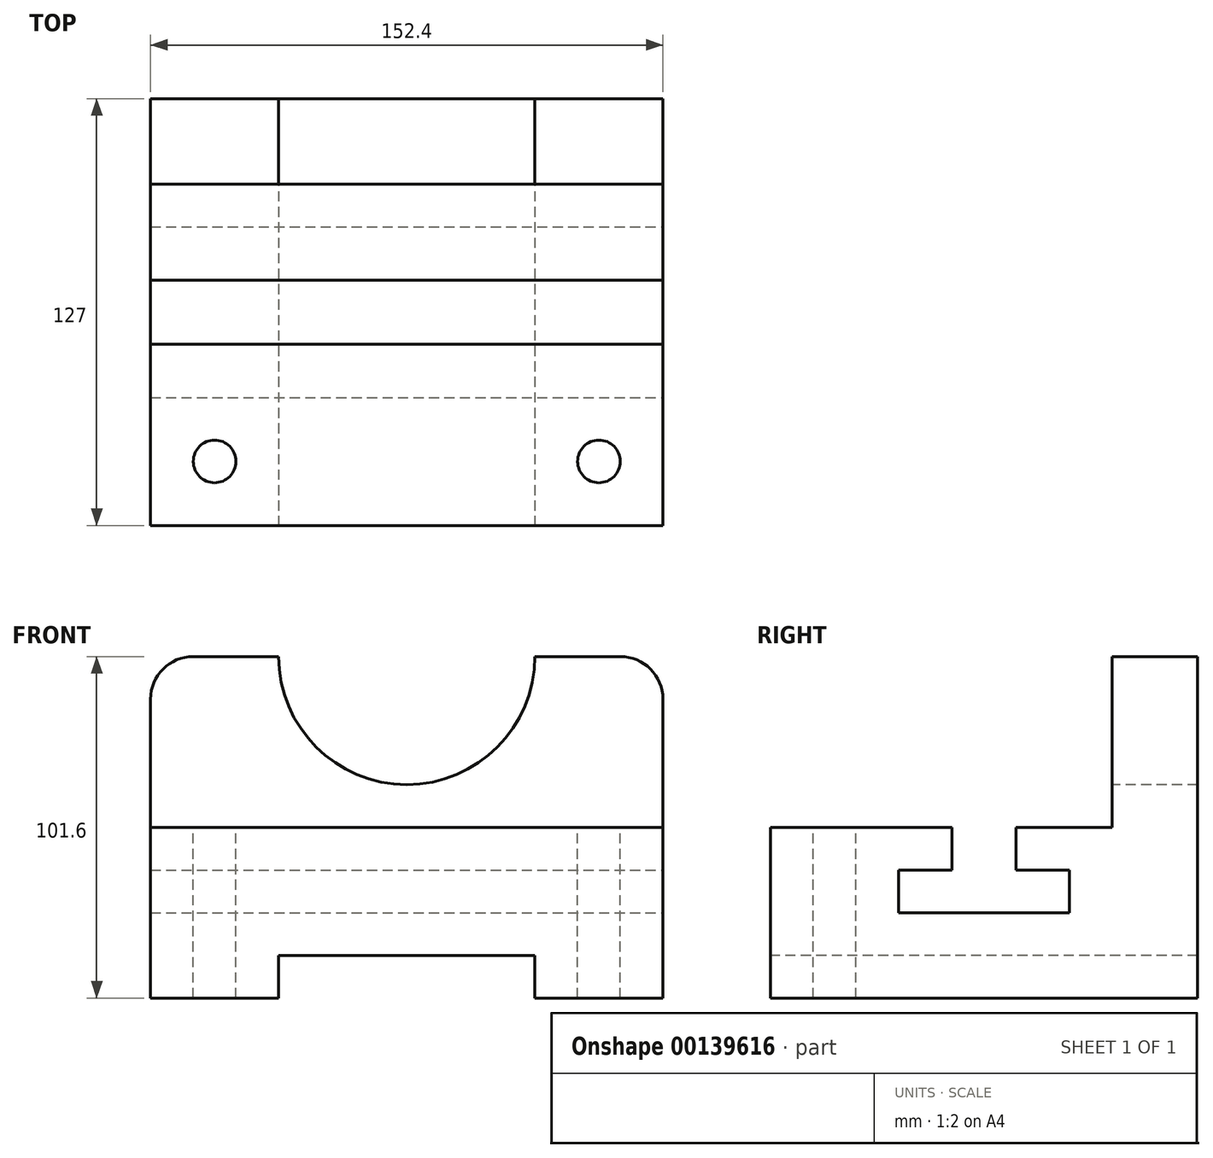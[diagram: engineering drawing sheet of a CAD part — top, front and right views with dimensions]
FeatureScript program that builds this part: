
annotation { "Feature Type Name" : "Feature", "Feature Type Description" : "" }
export const myFeature = defineFeature(function(context is Context, id is Id, definition is map)
    precondition{}
    {
        {
            var Q0;
            Q0=qCreatedBy(makeId("Front.planeOp"),FACE);
            var sketch = newSketch(context, id + "F0", { "sketchPlane" : qUnion([Q0])});
            skLineSegment(sketch, "E0", {"start": v(-76.3, 0) * mm, "end": v(76.1, 0) * mm});
            skLineSegment(sketch, "E1", {"start": v(76.1, 0) * mm, "end": v(76.1, 50.8) * mm});
            skLineSegment(sketch, "E2", {"start": v(76.1, 50.8) * mm, "end": v(-76.3, 50.8) * mm});
            skLineSegment(sketch, "E3", {"start": v(-76.3, 50.8) * mm, "end": v(-76.3, 0) * mm});
            skSolve(sketch);
        }
        {
            var Q0;
            Q0 = qSketchRegion(id + "F0", true);
            extrude(context, id + "F1", {"entities" : qUnion([Q0]), "endBound" : BoundingType.SYMMETRIC, "depth" : 127 * mm});
        }
        {
            var Q0;
            Q0=makeQuery(id+"F1.opExtrude","CAP_FACE",FACE,{"disambiguationData":[OSD([sQuery(id+"F0.wireOp",EDGE,"E0"),sQuery(id+"F0.wireOp",EDGE,"E1"),sQuery(id+"F0.wireOp",EDGE,"E2"),sQuery(id+"F0.wireOp",EDGE,"E3")])],"isStart":false});
            var sketch = newSketch(context, id + "F2", { "sketchPlane" : qUnion([Q0])});
            skLineSegment(sketch, "E4", {"start": v(-76.3, 0) * mm, "end": v(-38.2, 0) * mm});
            skLineSegment(sketch, "E5", {"start": v(76.1, 0) * mm, "end": v(38, 0) * mm});
            skLineSegment(sketch, "E6", {"start": v(38, 0) * mm, "end": v(-38.2, 0) * mm});
            skLineSegment(sketch, "E7", {"start": v(-38.2, 0) * mm, "end": v(-38.2, 12.7) * mm});
            skLineSegment(sketch, "E8", {"start": v(38, 0) * mm, "end": v(38, 12.7) * mm});
            skLineSegment(sketch, "E9", {"start": v(-38.2, 12.7) * mm, "end": v(38, 12.7) * mm});
            skSolve(sketch);
        }
        {
            var Q0;
            Q0 = qSketchRegion(id + "F2", true);
            extrude(context, id + "F3", {"entities" : qUnion([Q0]), "operationType" : NewBodyOperationType.REMOVE, "endBound" : BoundingType.THROUGH_ALL, "oppositeDirection" : true, "depth" : 38.1 * mm});
        }
        {
            var Q0;
            Q0=makeQuery(id+"F1.opExtrude","SWEPT_FACE",FACE,{"disambiguationData":[OSD([sQuery(id+"F0.wireOp",EDGE,"E1")])]});
            var sketch = newSketch(context, id + "F4", { "sketchPlane" : qUnion([Q0])});
            skLineSegment(sketch, "E10", {"start": v(-63.5, 0) * mm, "end": v(-25.4, 0) * mm});
            skLineSegment(sketch, "E11", {"start": v(-25.4, 0) * mm, "end": v(-25.4, 25.4) * mm});
            skLineSegment(sketch, "E12", {"start": v(-25.4, 0) * mm, "end": v(25.4, 0) * mm});
            skLineSegment(sketch, "E13", {"start": v(25.4, 0) * mm, "end": v(25.4, 25.4) * mm});
            skLineSegment(sketch, "E14", {"start": v(-25.4, 25.4) * mm, "end": v(25.4, 25.4) * mm});
            skLineSegment(sketch, "E15", {"start": v(-25.4, 25.4) * mm, "end": v(-25.4, 38.1) * mm});
            skLineSegment(sketch, "E16", {"start": v(25.4, 25.4) * mm, "end": v(25.4, 38.1) * mm});
            skLineSegment(sketch, "E17", {"start": v(-25.4, 38.1) * mm, "end": v(-9.53, 38.1) * mm});
            skLineSegment(sketch, "E18", {"start": v(25.4, 38.1) * mm, "end": v(9.52, 38.1) * mm});
            skLineSegment(sketch, "E19", {"start": v(-9.53, 38.1) * mm, "end": v(-9.53, 50.8) * mm});
            skLineSegment(sketch, "E20", {"start": v(9.52, 38.1) * mm, "end": v(9.53, 50.8) * mm});
            skLineSegment(sketch, "E21", {"start": v(9.53, 50.8) * mm, "end": v(-9.53, 50.8) * mm});
            skSolve(sketch);
        }
        {
            var Q0;
            Q0=makeQuery(id+"F4.imprint","IMPRINT",FACE,{"disambiguationData":[TD([[makeQuery(id+"F4.imprint","IMPRINT",EDGE,{"derivedFrom":sQuery(id+"F4.wireOp",EDGE,"E14")}),1.0]])]});
            var Q1;
            Q1=makeQuery(id+"F1.opExtrude","SWEPT_FACE",FACE,{"disambiguationData":[OSD([sQuery(id+"F0.wireOp",EDGE,"E3")])]});
            extrude(context, id + "F5", {"entities" : qUnion([Q0]), "operationType" : NewBodyOperationType.REMOVE, "endBound" : BoundingType.UP_TO_SURFACE, "oppositeDirection" : true, "endBoundEntityFace" : qUnion([Q1]), "depth" : 25.4 * mm});
        }
        {
            var Q0;
            Q0=makeQuery(id+"F1.opExtrude","SWEPT_FACE",FACE,{"disambiguationData":[OSD([sQuery(id+"F0.wireOp",EDGE,"E1")])]});
            var sketch = newSketch(context, id + "F6", { "sketchPlane" : qUnion([Q0])});
            skLineSegment(sketch, "E22", {"start": v(63.5, 50.8) * mm, "end": v(63.5, 101.6) * mm});
            skLineSegment(sketch, "E23", {"start": v(63.5, 101.6) * mm, "end": v(38.1, 101.6) * mm});
            skLineSegment(sketch, "E24", {"start": v(38.1, 101.6) * mm, "end": v(38.1, 50.8) * mm});
            skPoint(sketch, "E24.endSnap0", {"position": v(36.51, 50.8) * mm});
            skLineSegment(sketch, "E25", {"start": v(38.1, 50.8) * mm, "end": v(63.5, 50.8) * mm});
            skSolve(sketch);
        }
        {
            var Q0;
            Q0 = qSketchRegion(id + "F6", true);
            var Q1;
            Q1=makeQuery(id+"F1.opExtrude","SWEPT_FACE",FACE,{"disambiguationData":[OSD([sQuery(id+"F0.wireOp",EDGE,"E3")])]});
            extrude(context, id + "F7", {"entities" : qUnion([Q0]), "operationType" : NewBodyOperationType.ADD, "endBound" : BoundingType.UP_TO_SURFACE, "oppositeDirection" : true, "endBoundEntityFace" : qUnion([Q1]), "depth" : 25.4 * mm});
        }
        {
            var Q0;
            Q0=makeQuery(id+"F7.opExtrude","SWEPT_FACE",FACE,{"disambiguationData":[OSD([sQuery(id+"F6.wireOp",EDGE,"E24")])]});
            var sketch = newSketch(context, id + "F8", { "sketchPlane" : qUnion([Q0])});
            skArc(sketch, "E26", {"start": v(-38.2, 101.6) * mm, "mid": v(-0.1, 63.5) * mm, "end": v(38, 101.6) * mm});
            skLineSegment(sketch, "E27.0", {"start": v(-38.2, 101.6) * mm, "end": v(38, 101.6) * mm});
            skPoint(sketch, "E28.orphan", {"position": v(-76.3, 101.6) * mm});
            skPoint(sketch, "E29.orphan", {"position": v(76.1, 101.6) * mm});
            skSolve(sketch);
        }
        {
            var Q0;
            Q0 = qSketchRegion(id + "F8", true);
            var Q1;
            Q1=makeQuery(id+"F8.imprint","IMPRINT",FACE,{"disambiguationData":[TD([[makeQuery(id+"F8.imprint","IMPRINT",EDGE,{"derivedFrom":sQuery(id+"F8.wireOp",EDGE,"E26")}),1.0]])]});
            var Q2;
            Q2=makeQuery(id+"F7.boolean.opBoolean","MERGE",FACE,{"derivedFrom":[makeQuery(id+"F1.opExtrude","CAP_FACE",FACE,{"disambiguationData":[OSD([sQuery(id+"F0.wireOp",EDGE,"E0"),sQuery(id+"F0.wireOp",EDGE,"E1"),sQuery(id+"F0.wireOp",EDGE,"E2"),sQuery(id+"F0.wireOp",EDGE,"E3")])],"isStart":true}),makeQuery(id+"F7.opExtrude","SWEPT_FACE",FACE,{"disambiguationData":[OSD([sQuery(id+"F6.wireOp",EDGE,"E22")])]})]});
            extrude(context, id + "F9", {"entities" : qUnion([Q0, Q1]), "operationType" : NewBodyOperationType.REMOVE, "endBound" : BoundingType.UP_TO_SURFACE, "oppositeDirection" : true, "endBoundEntityFace" : qUnion([Q2]), "depth" : 15.45 * mm});
        }
        {
            var Q0;
            Q0=makeQuery(id+"F7.opExtrude","CAP_EDGE",EDGE,{"disambiguationData":[OSD([sQuery(id+"F6.wireOp",EDGE,"E23")])],"isStart":false});
            fillet(context, id + "F10", {"entities" : qUnion([Q0]), "radius" : 12.7 * mm, "tangentPropagation" : true, "allowEdgeOverflow" : false});
        }
        {
            var Q0;
            Q0=makeQuery(id+"F7.opExtrude","CAP_EDGE",EDGE,{"disambiguationData":[OSD([sQuery(id+"F6.wireOp",EDGE,"E23")])],"isStart":true});
            fillet(context, id + "F11", {"entities" : qUnion([Q0]), "radius" : 12.7 * mm, "tangentPropagation" : true, "allowEdgeOverflow" : false});
        }
        {
            var Q0;
            {var subQ1=sQuery(id+"F0.wireOp",EDGE,"E2");Q0=makeQuery(id+"F5.boolean.opBoolean","SPLIT",FACE,{"disambiguationData":[TD([makeQuery(id+"F5.opExtrude","SWEPT_FACE",FACE,{"disambiguationData":[OSD([sQuery(id+"F4.wireOp",EDGE,"E19")])]})])],"derivedFrom":makeQuery(id+"F1.opExtrude","SWEPT_FACE",FACE,{"disambiguationData":[OSD([subQ1])]})});}
            var sketch = newSketch(context, id + "F12", { "sketchPlane" : qUnion([Q0])});
            skCircle(sketch, "E30", {"center": v(-57.25, -44.45) * mm, "radius": 6.35 * mm});
            skCircle(sketch, "E31", {"center": v(57.05, -44.45) * mm, "radius": 6.35 * mm});
            skPoint(sketch, "E32.orphan", {"position": v(76.1, -44.45) * mm});
            skSolve(sketch);
        }
        {
            var Q0;
            Q0 = qSketchRegion(id + "F12", true);
            var Q1;
            Q1=makeQuery(id+"F12.imprint","IMPRINT",FACE,{"disambiguationData":[TD([[makeQuery(id+"F12.imprint","IMPRINT",EDGE,{"derivedFrom":sQuery(id+"F12.wireOp",EDGE,"E30")}),1.0]])]});
            var Q2;
            Q2=makeQuery(id+"F1.opExtrude","SWEPT_FACE",FACE,{"disambiguationData":[OSD([sQuery(id+"F0.wireOp",EDGE,"E0")])]});
            extrude(context, id + "F13", {"entities" : qUnion([Q0, Q1]), "operationType" : NewBodyOperationType.REMOVE, "endBound" : BoundingType.UP_TO_SURFACE, "oppositeDirection" : true, "endBoundEntityFace" : qUnion([Q2]), "depth" : 25.4 * mm});
        }
    });
